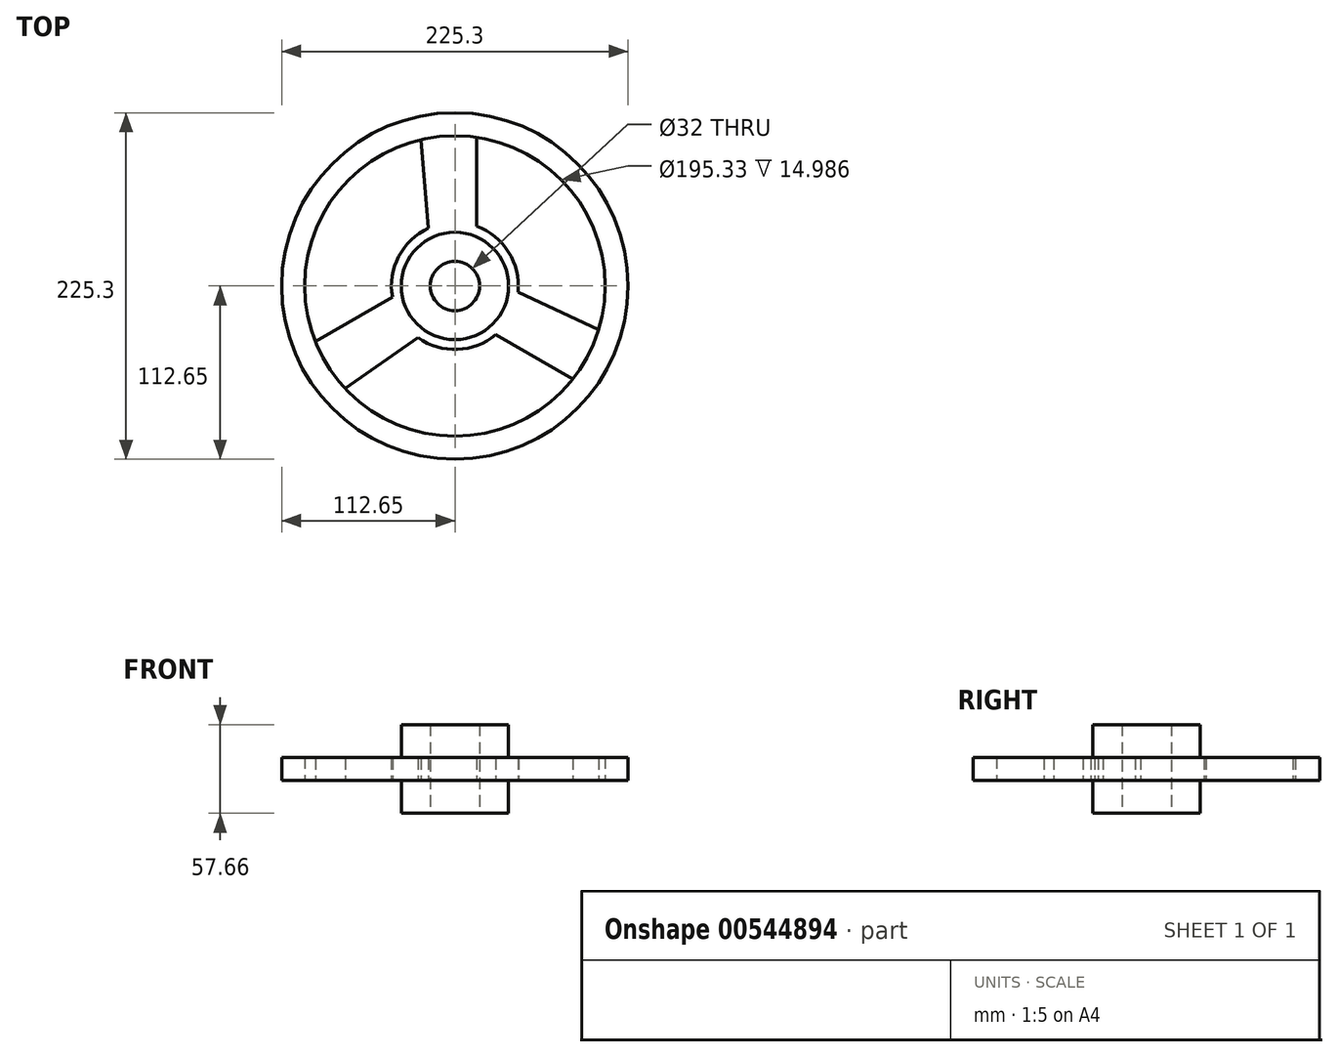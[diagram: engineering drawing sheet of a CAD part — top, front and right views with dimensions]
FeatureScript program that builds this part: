
annotation { "Feature Type Name" : "Feature", "Feature Type Description" : "" }
export const myFeature = defineFeature(function(context is Context, id is Id, definition is map)
    precondition{}
    {
        {
            var Q0;
            Q0=qCreatedBy(makeId("Top.planeOp"),FACE);
            var sketch = newSketch(context, id + "F0", { "sketchPlane" : qUnion([Q0])});
            skCircle(sketch, "E0", {"center": v(0, 0) * mm, "radius": 41.28 * mm});
            skPoint(sketch, "E1.center", {"position": v(1.66, -8.03) * mm});
            skCircle(sketch, "E2", {"center": v(0, 0) * mm, "radius": 16 * mm});
            skCircle(sketch, "E3", {"center": v(0, 0) * mm, "radius": 34.93 * mm});
            skCircle(sketch, "E4", {"center": v(0, 0) * mm, "radius": 97.66 * mm});
            skCircle(sketch, "E5", {"center": v(0, 0) * mm, "radius": 112.65 * mm});
            skLineSegment(sketch, "E6", {"start": v(14.08, 96.64) * mm, "end": v(14.08, 38.8) * mm});
            skLineSegment(sketch, "E7", {"start": v(-22.05, 95.14) * mm, "end": v(-17.18, 37.53) * mm});
            skLineSegment(sketch, "E8.1.0", {"start": v(-71.37, -66.66) * mm, "end": v(-23.9, -33.64) * mm});
            skLineSegment(sketch, "E8.2.0", {"start": v(93.42, -28.48) * mm, "end": v(41.1, -3.88) * mm});
            skLineSegment(sketch, "E9.1.0", {"start": v(-90.74, -36.12) * mm, "end": v(-40.64, -7.2) * mm});
            skLineSegment(sketch, "E9.2.0", {"start": v(76.65, -60.52) * mm, "end": v(26.56, -31.6) * mm});
            skSolve(sketch);
        }
        {
            var Q0;
            Q0=makeQuery(id+"F0.imprint","IMPRINT",FACE,{"disambiguationData":[TD([[makeQuery(id+"F0.imprint","IMPRINT",EDGE,{"derivedFrom":sQuery(id+"F0.wireOp",EDGE,"E2")}),-1.0]])]});
            extrude(context, id + "F1", {"entities" : qUnion([Q0]), "endBound" : BoundingType.SYMMETRIC, "depth" : 57.66 * mm, "offsetDistance" : 25.4 * mm});
        }
        {
            var Q0;
            Q0=makeQuery(id+"F0.imprint","IMPRINT",FACE,{"disambiguationData":[TD([[makeQuery(id+"F0.imprint","IMPRINT",EDGE,{"derivedFrom":sQuery(id+"F0.wireOp",EDGE,"E3")}),-1.0]])]});
            var Q1;
            {var subQ0=sQuery(id+"F0.wireOp",EDGE,"E6");Q1=makeQuery(id+"F0.imprint","IMPRINT",FACE,{"disambiguationData":[TD([[makeQuery(id+"F0.imprint","IMPRINT",EDGE,{"derivedFrom":subQ0}),-1.0]])]});}
            var Q2;
            {var subQ0=sQuery(id+"F0.wireOp",EDGE,"E8.1.0");Q2=makeQuery(id+"F0.imprint","IMPRINT",FACE,{"disambiguationData":[TD([[makeQuery(id+"F0.imprint","IMPRINT",EDGE,{"derivedFrom":subQ0}),1.0]])]});}
            var Q3;
            {var subQ0=sQuery(id+"F0.wireOp",EDGE,"E8.2.0");Q3=makeQuery(id+"F0.imprint","IMPRINT",FACE,{"disambiguationData":[TD([[makeQuery(id+"F0.imprint","IMPRINT",EDGE,{"derivedFrom":subQ0}),1.0]])]});}
            extrude(context, id + "F2", {"entities" : qUnion([Q0, Q1, Q2, Q3]), "operationType" : NewBodyOperationType.ADD, "endBound" : BoundingType.SYMMETRIC, "depth" : 14.22 * mm, "offsetDistance" : 25.4 * mm});
        }
        {
            var Q0;
            Q0=makeQuery(id+"F0.imprint","IMPRINT",FACE,{"disambiguationData":[TD([[makeQuery(id+"F0.imprint","IMPRINT",EDGE,{"derivedFrom":sQuery(id+"F0.wireOp",EDGE,"E5")}),1.0]])]});
            extrude(context, id + "F3", {"entities" : qUnion([Q0]), "operationType" : NewBodyOperationType.ADD, "endBound" : BoundingType.SYMMETRIC, "depth" : 15 * mm, "offsetDistance" : 25.4 * mm});
        }
    });
